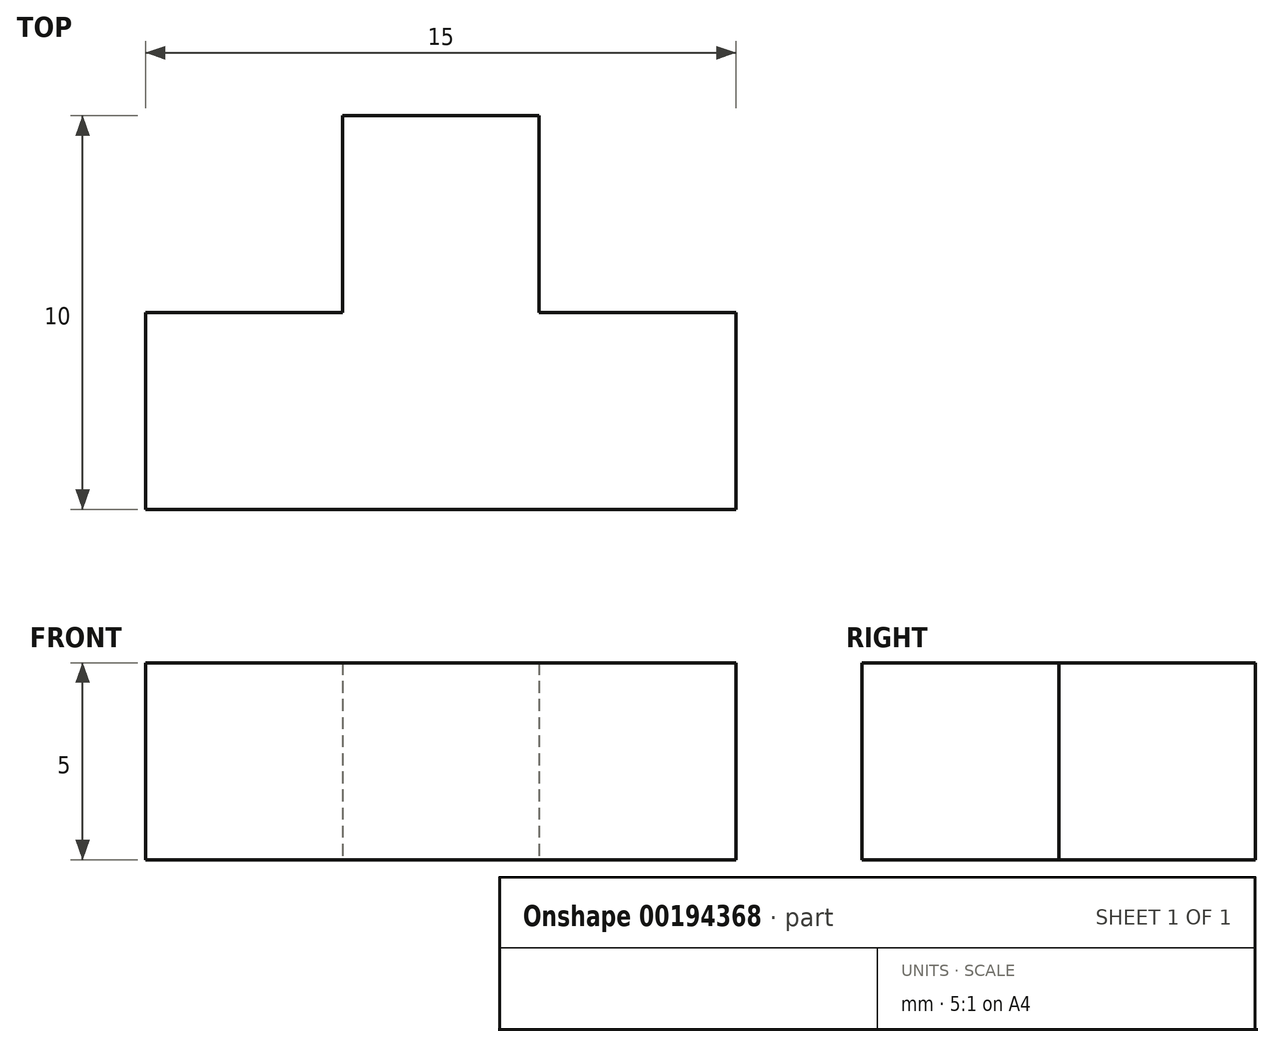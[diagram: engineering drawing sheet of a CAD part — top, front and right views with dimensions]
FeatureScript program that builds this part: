
annotation { "Feature Type Name" : "Feature", "Feature Type Description" : "" }
export const myFeature = defineFeature(function(context is Context, id is Id, definition is map)
    precondition{}
    {
        {
            var Q0;
            Q0=qCreatedBy(makeId("Top.planeOp"),FACE);
            var sketch = newSketch(context, id + "F0", { "sketchPlane" : qUnion([Q0])});
            skLineSegment(sketch, "E0.bottom", {"start": v(-2.5, 2.5) * mm, "end": v(2.5, 2.5) * mm});
            skLineSegment(sketch, "E0.top", {"start": v(-2.5, -2.5) * mm, "end": v(2.5, -2.5) * mm});
            skLineSegment(sketch, "E0.left", {"start": v(-2.5, 2.5) * mm, "end": v(-2.5, -2.5) * mm});
            skLineSegment(sketch, "E0.right", {"start": v(2.5, 2.5) * mm, "end": v(2.5, -2.5) * mm});
            skPoint(sketch, "E0.middle", {"position": v(0, 0) * mm});
            skLineSegment(sketch, "E1.bottom", {"start": v(-7.5, -7.5) * mm, "end": v(7.5, -7.5) * mm});
            skLineSegment(sketch, "E1.top", {"start": v(-7.5, -2.5) * mm, "end": v(7.5, -2.5) * mm});
            skLineSegment(sketch, "E1.left", {"start": v(-7.5, -7.5) * mm, "end": v(-7.5, -2.5) * mm});
            skLineSegment(sketch, "E1.right", {"start": v(7.5, -7.5) * mm, "end": v(7.5, -2.5) * mm});
            skPoint(sketch, "E2", {"position": v(0, -2.5) * mm});
            skSolve(sketch);
        }
        {
            var Q0;
            Q0 = qSketchRegion(id + "F0", true);
            extrude(context, id + "F1", {"entities" : qUnion([Q0]), "depth" : 5 * mm});
        }
    });
